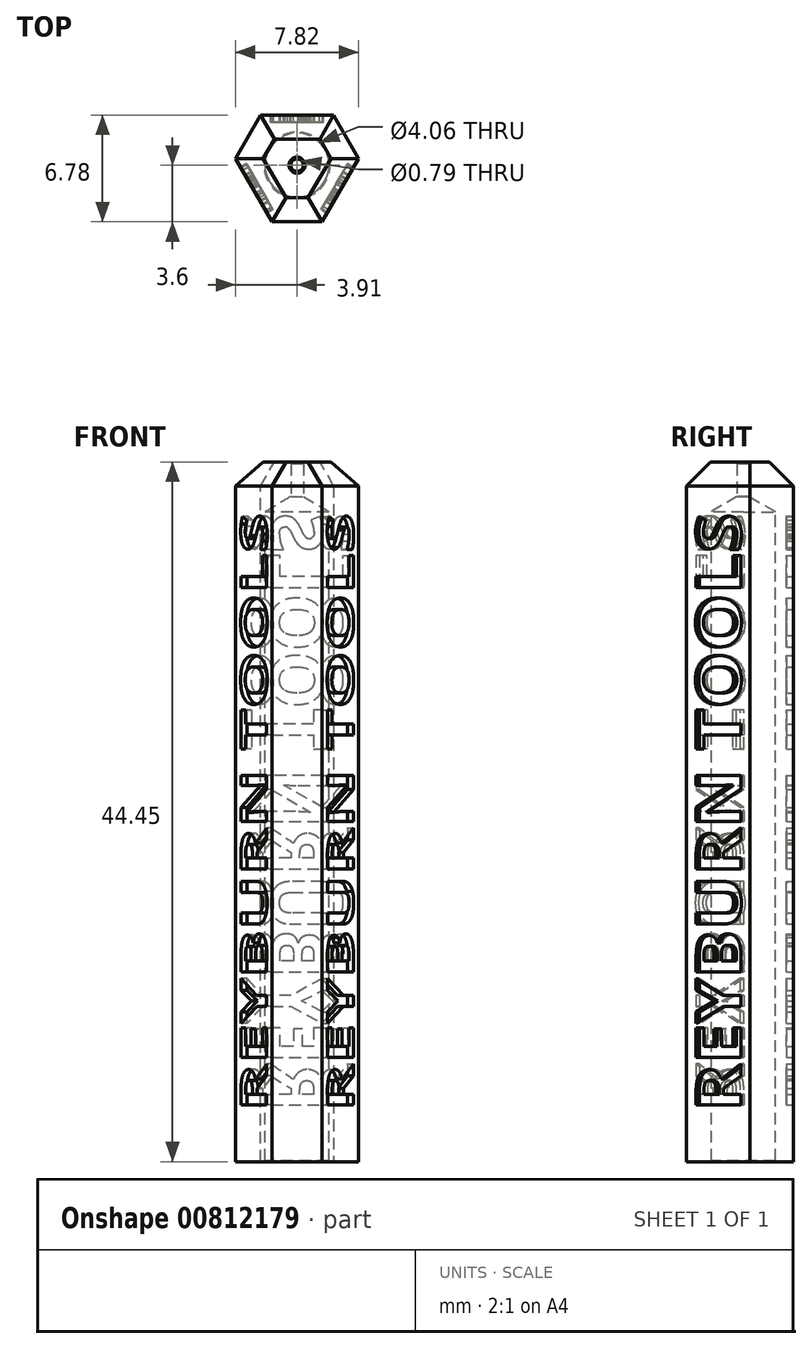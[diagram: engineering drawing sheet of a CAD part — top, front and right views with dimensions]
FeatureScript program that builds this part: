
annotation { "Feature Type Name" : "Feature", "Feature Type Description" : "" }
export const myFeature = defineFeature(function(context is Context, id is Id, definition is map)
    precondition{}
    {
        {
            var Q0;
            Q0=qCreatedBy(makeId("Top.planeOp"),FACE);
            var sketch = newSketch(context, id + "F0", { "sketchPlane" : qUnion([Q0])});
            skCircle(sketch, "E0.cCircle", {"center": v(0, 0) * mm, "radius": 6.35 * mm, "construction": true});
            skLineSegment(sketch, "E0.0", {"start": v(0, -6.35) * mm, "end": v(-5.5, 3.17) * mm});
            skLineSegment(sketch, "E0.1", {"start": v(-5.5, 3.18) * mm, "end": v(5.5, 3.18) * mm});
            skLineSegment(sketch, "E0.2", {"start": v(5.5, 3.18) * mm, "end": v(0, -6.35) * mm});
            skSolve(sketch);
        }
        {
            var Q0;
            Q0=makeQuery(id+"F0.imprint","IMPRINT",FACE,{"disambiguationData":[TD([[makeQuery(id+"F0.imprint","IMPRINT",EDGE,{"derivedFrom":sQuery(id+"F0.wireOp",EDGE,"E0.0")}),-1.0]])]});
            extrude(context, id + "F1", {"entities" : qUnion([Q0]), "oppositeDirection" : true, "depth" : 44.45 * mm, "offsetDistance" : 25.4 * mm});
        }
        {
            var Q0;
            Q0=makeQuery(id+"F1.opExtrude","CAP_FACE",FACE,{"disambiguationData":[OSD([sQuery(id+"F0.wireOp",EDGE,"E0.0"),sQuery(id+"F0.wireOp",EDGE,"E0.1"),sQuery(id+"F0.wireOp",EDGE,"E0.2")])],"isStart":false});
            var sketch = newSketch(context, id + "F2", { "sketchPlane" : qUnion([Q0])});
            skPoint(sketch, "E1", {"position": v(0, 0) * mm});
            skSolve(sketch);
        }
        {
            var Q0;
            Q0=sQuery(id+"F2.wireOp",VERTEX,"E1");
            var Q1;
            Q1=makeQuery(id+"F1.opExtrude","SWEPT_BODY",BODY,{"disambiguationData":[OSD([sQuery(id+"F0.wireOp",EDGE,"ghmTZ7Fa-hntI-yseL-cm0A-BedO1wdsdYtG")])]});
            var Q2;
            Q2=makeQuery(id+"F1.opExtrude","SWEPT_BODY",BODY,{"disambiguationData":[OSD([sQuery(id+"F0.wireOp",EDGE,"E0.0"),sQuery(id+"F0.wireOp",EDGE,"E0.1"),sQuery(id+"F0.wireOp",EDGE,"E0.2")])]});
            hole(context, id + "F3", {"style" : HoleStyle.C_SINK, "endStyle" : HoleEndStyle.BLIND, "holeDiameter" : 4.06 * mm, "cSinkDiameter" : 4.2 * mm, "cSinkAngle" : 90 * degree, "majorDiameter" : 6.35 * mm, "holeDepth" : 41.27 * mm, "isTappedThrough" : true, "tappedDepth" : 12.7 * mm, "tapClearance" : 3, "locations" : qUnion([Q0]), "scope" : qUnion([Q1, Q2]), "startStyle" : HoleStartStyle.PART});
        }
        {
            var Q0;
            Q0=makeQuery(id+"F1.opExtrude","SWEPT_EDGE",EDGE,{"disambiguationData":[OSD([sQuery(id+"F0.wireOp",EDGE,"E0.0"),sQuery(id+"F0.wireOp",EDGE,"E0.2")])]});
            var Q1;
            Q1=makeQuery(id+"F1.opExtrude","SWEPT_EDGE",EDGE,{"disambiguationData":[OSD([sQuery(id+"F0.wireOp",EDGE,"E0.1"),sQuery(id+"F0.wireOp",EDGE,"E0.2")])]});
            var Q2;
            Q2=makeQuery(id+"F1.opExtrude","SWEPT_EDGE",EDGE,{"disambiguationData":[OSD([sQuery(id+"F0.wireOp",EDGE,"E0.0"),sQuery(id+"F0.wireOp",EDGE,"E0.1")])]});
            chamfer(context, id + "F4", {"entities" : qUnion([Q0, Q1, Q2]), "width" : 3.17 * mm, "tangentPropagation" : true});
        }
        {
            var Q0;
            Q0=makeQuery(id+"F1.opExtrude","SWEPT_FACE",FACE,{"disambiguationData":[OSD([sQuery(id+"F0.wireOp",EDGE,"E0.1")])]});
            var sketch = newSketch(context, id + "F5", { "sketchPlane" : qUnion([Q0])});
            skText(sketch, "E2", { "text": "REYBURN TOOLS", "fontName": "OpenSans-Bold.ttf"});
            skLineSegment(sketch, "E3", {"start": v(0, 0) * mm, "end": v(0, -3.18) * mm, "construction": true});
            const initialGuessF5  = {"E2": [0.00165, -0.04127, 0, 1, 0.0033]};
            skSetInitialGuess(sketch, initialGuessF5);
            skSolve(sketch);
        }
        {
            var Q0;
            Q0 = qSketchRegion(id + "F5", true);
            var Q1;
            Q1 = qSketchRegion(id + "F7", true);
            extrude(context, id + "F6", {"entities" : qUnion([Q0, Q1]), "operationType" : NewBodyOperationType.REMOVE, "oppositeDirection" : true, "depth" : 0.43 * mm, "offsetDistance" : 25.4 * mm});
        }
        {
            var Q0;
            Q0=makeQuery(id+"F1.opExtrude","SWEPT_FACE",FACE,{"disambiguationData":[OSD([sQuery(id+"F0.wireOp",EDGE,"E0.0")])]});
            var sketch = newSketch(context, id + "F7", { "sketchPlane" : qUnion([Q0])});
            skText(sketch, "E4", { "text": "REYBURN TOOLS", "fontName": "OpenSans-Bold.ttf"});
            skLineSegment(sketch, "E5", {"start": v(0, 0) * mm, "end": v(0, -3.18) * mm, "construction": true});
            const initialGuessF7  = {"E4": [0.00165, -0.04127, 0, 1, 0.0033]};
            skSetInitialGuess(sketch, initialGuessF7);
            skSolve(sketch);
        }
        {
            var Q0;
            Q0 = qSketchRegion(id + "F7", true);
            extrude(context, id + "F8", {"entities" : qUnion([Q0]), "operationType" : NewBodyOperationType.REMOVE, "oppositeDirection" : true, "depth" : 0.43 * mm, "offsetDistance" : 25.4 * mm});
        }
        {
            var Q0;
            Q0=makeQuery(id+"F1.opExtrude","SWEPT_FACE",FACE,{"disambiguationData":[OSD([sQuery(id+"F0.wireOp",EDGE,"E0.2")])]});
            var sketch = newSketch(context, id + "F9", { "sketchPlane" : qUnion([Q0])});
            skText(sketch, "E6", { "text": "REYBURN TOOLS", "fontName": "OpenSans-Bold.ttf"});
            skLineSegment(sketch, "E7", {"start": v(0, 0) * mm, "end": v(0, -3.18) * mm, "construction": true});
            const initialGuessF9  = {"E6": [0.00165, -0.04127, 0, 1, 0.0033]};
            skSetInitialGuess(sketch, initialGuessF9);
            skSolve(sketch);
        }
        {
            var Q0;
            Q0 = qSketchRegion(id + "F9", true);
            extrude(context, id + "F10", {"entities" : qUnion([Q0]), "operationType" : NewBodyOperationType.REMOVE, "oppositeDirection" : true, "depth" : 0.43 * mm, "offsetDistance" : 25.4 * mm});
        }
        {
            var Q0;
            Q0=makeQuery(id+"F1.opExtrude","CAP_FACE",FACE,{"disambiguationData":[OSD([sQuery(id+"F0.wireOp",EDGE,"E0.0"),sQuery(id+"F0.wireOp",EDGE,"E0.1"),sQuery(id+"F0.wireOp",EDGE,"E0.2")])],"isStart":true});
            var sketch = newSketch(context, id + "F11", { "sketchPlane" : qUnion([Q0])});
            skPoint(sketch, "E8", {"position": v(0, 0) * mm});
            skSolve(sketch);
        }
        {
            var Q0;
            Q0=sQuery(id+"F11.wireOp",VERTEX,"E8");
            var Q1;
            Q1=makeQuery(id+"F1.opExtrude","SWEPT_BODY",BODY,{"disambiguationData":[OSD([sQuery(id+"F0.wireOp",EDGE,"E0.0"),sQuery(id+"F0.wireOp",EDGE,"E0.1"),sQuery(id+"F0.wireOp",EDGE,"E0.2")])]});
            hole(context, id + "F12", {"style" : HoleStyle.C_SINK, "endStyle" : HoleEndStyle.THROUGH, "holeDiameter" : 0.8 * mm, "cSinkDiameter" : 1.02 * mm, "cSinkAngle" : 90 * degree, "majorDiameter" : 6.35 * mm, "isTappedThrough" : true, "tappedDepth" : 12.7 * mm, "tapClearance" : 3, "locations" : qUnion([Q0]), "scope" : qUnion([Q1]), "startStyle" : HoleStartStyle.PART});
        }
        {
            var Q0;
            Q0=makeQuery(id+"F1.opExtrude","CAP_EDGE",EDGE,{"disambiguationData":[OSD([sQuery(id+"F0.wireOp",EDGE,"E0.2")])],"isStart":true});
            var Q1;
            {var subQ0=sQuery(id+"F0.wireOp",EDGE,"E0.2");var subQ1=sQuery(id+"F0.wireOp",EDGE,"E0.0");Q1=makeQuery(id+"F4.opChamfer","BLEND_EDGE",EDGE,{"blendedFrom":[makeQuery(id+"F1.opExtrude","SWEPT_EDGE",EDGE,{"disambiguationData":[OSD([subQ1,subQ0])]}),makeQuery(id+"F1.opExtrude","CAP_FACE",FACE,{"disambiguationData":[OSD([subQ1,sQuery(id+"F0.wireOp",EDGE,"E0.1"),subQ0])],"isStart":true})],"blendedInto":[makeQuery(id+"F1.opExtrude","CAP_FACE",FACE,{"disambiguationData":[OSD([subQ1,sQuery(id+"F0.wireOp",EDGE,"E0.1"),subQ0])],"isStart":true})]});}
            var Q2;
            Q2=makeQuery(id+"F1.opExtrude","CAP_EDGE",EDGE,{"disambiguationData":[OSD([sQuery(id+"F0.wireOp",EDGE,"E0.0")])],"isStart":true});
            var Q3;
            {var subQ0=sQuery(id+"F0.wireOp",EDGE,"E0.1");var subQ1=sQuery(id+"F0.wireOp",EDGE,"E0.0");Q3=makeQuery(id+"F4.opChamfer","BLEND_EDGE",EDGE,{"blendedFrom":[makeQuery(id+"F1.opExtrude","SWEPT_EDGE",EDGE,{"disambiguationData":[OSD([subQ1,subQ0])]}),makeQuery(id+"F1.opExtrude","CAP_FACE",FACE,{"disambiguationData":[OSD([subQ1,subQ0,sQuery(id+"F0.wireOp",EDGE,"E0.2")])],"isStart":true})],"blendedInto":[makeQuery(id+"F1.opExtrude","CAP_FACE",FACE,{"disambiguationData":[OSD([subQ1,subQ0,sQuery(id+"F0.wireOp",EDGE,"E0.2")])],"isStart":true})]});}
            var Q4;
            Q4=makeQuery(id+"F1.opExtrude","CAP_EDGE",EDGE,{"disambiguationData":[OSD([sQuery(id+"F0.wireOp",EDGE,"E0.1")])],"isStart":true});
            var Q5;
            {var subQ0=sQuery(id+"F0.wireOp",EDGE,"E0.2");var subQ1=sQuery(id+"F0.wireOp",EDGE,"E0.1");Q5=makeQuery(id+"F4.opChamfer","BLEND_EDGE",EDGE,{"blendedFrom":[makeQuery(id+"F1.opExtrude","SWEPT_EDGE",EDGE,{"disambiguationData":[OSD([subQ1,subQ0])]}),makeQuery(id+"F1.opExtrude","CAP_FACE",FACE,{"disambiguationData":[OSD([sQuery(id+"F0.wireOp",EDGE,"E0.0"),subQ1,subQ0])],"isStart":true})],"blendedInto":[makeQuery(id+"F1.opExtrude","CAP_FACE",FACE,{"disambiguationData":[OSD([sQuery(id+"F0.wireOp",EDGE,"E0.0"),subQ1,subQ0])],"isStart":true})]});}
            chamfer(context, id + "F13", {"entities" : qUnion([Q0, Q1, Q2, Q3, Q4, Q5]), "width" : 1.52 * mm, "tangentPropagation" : true});
        }
    });
